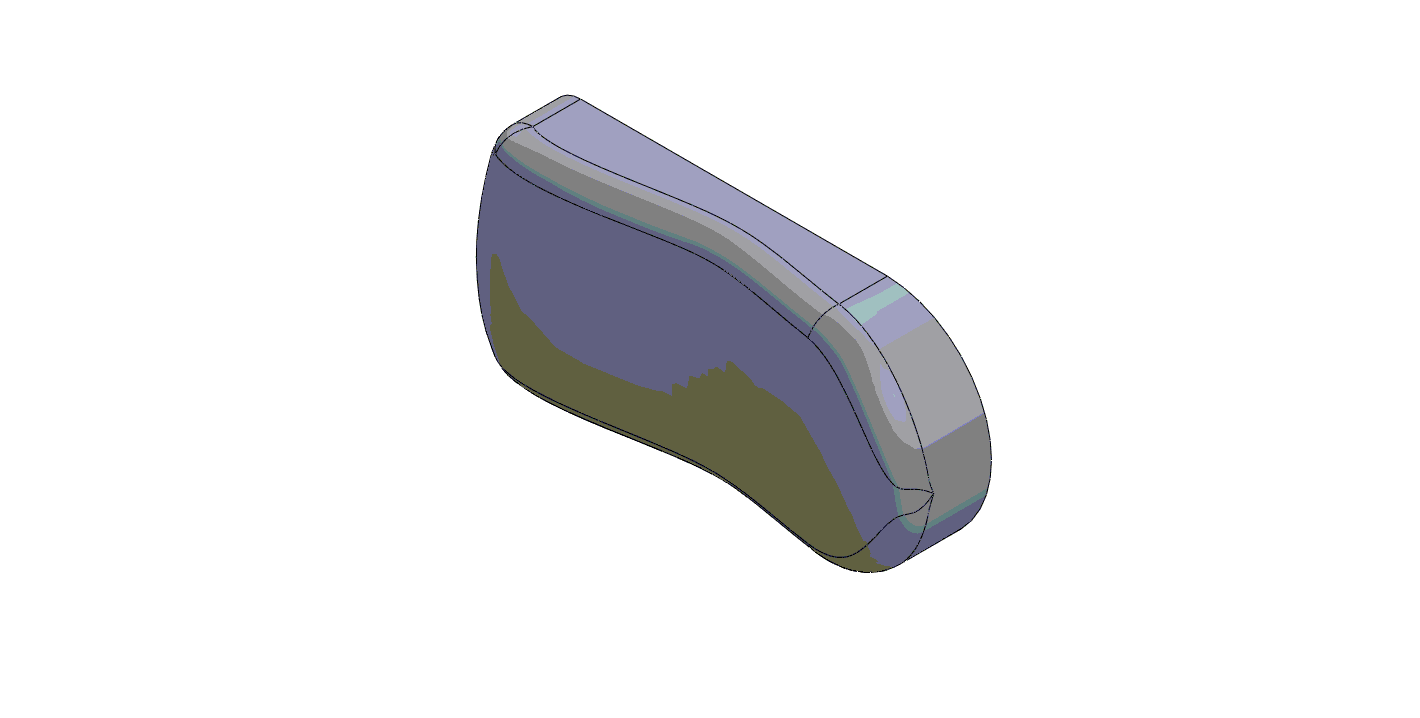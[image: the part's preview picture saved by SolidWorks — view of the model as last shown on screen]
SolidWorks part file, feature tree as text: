
SOLIDWORKS PART (.sldprt)
format: sldprt  version: not decoded by parser v0  size: 291,840 bytes
history: native  units: mm
features: sketch x6, extrude x3, cut_extrude x2, material x1, move_body x1, revolve x1, fillet x1 (+12 scaffold rows collapsed; 1 parser-record rows omitted)
feature tree (28):
  scaffold x12  (default folders/planes/origin — collapsed)
  material  "Material <not specified>"
  sketch  "Sketch1"  dims[D1=0.0mm D2=0.0mm]
  extrude  "Boss-Extrude1"  Depth=5mm
  sketch  "Sketch3"
  cut_extrude  "Cut-Extrude1"  Depth=10mm
  move_body  "Body-Move/Copy1"
  parser-record x1  (decoder bookkeeping rows leaked as tree rows — omitted from the tree; the rows remain in map.json)
  sketch  "Sketch4"
  extrude  "Boss-Extrude2"  Depth=5mm
  sketch  "Sketch5"  dims[D1=2.5mm]
  revolve  "Revolve2"  [1 undecoded]
  sketch  "Sketch9"  dims[D1=0.0mm]
  extrude  "Boss-Extrude3"  [1 undecoded]
  sketch  "Sketch10"  dims[D1=0.0mm]
  cut_extrude  "Cut-Extrude2"  Depth=47mm
  fillet  "Fillet1"  Radius=5mm
decode coverage: 9 of 14 modeling features carry decoded parameters
note: 2 parameter values undecoded
note: suppression state not decoded; provenance and decode notes live in map.json
